# Revit family: ido_seven_d_5650047_arm_001
name_source: partatom
category: Plumbing Fixtures
revit_build: Autodesk Revit 2018 (Build: 20170223_1515(x64)
units: mm (PartAtom-declared; Revit-internal decimal feet)

## family parameters
Always vertical = Yes
Cut with Voids When Loaded = No
Part Type = Normal
Room Calculation Point = No
Round Connector Dimension = Use Radius
Shared = No
Work Plane-Based = No

## types (1)
- ido_seven_d_5650047_arm_001
    Description = connector geom / spherical cord
    MC_R = 55 mm
    Material 1 = Mat1
    RfaVersion = 1.0
    Waste Connection = Yes
    cncShiftX_ = 10000 mm  [stored 32.8084 ft]
    cncShiftY_ = 10000 mm  [stored 32.8084 ft]
    cncShiftZ_ = 10000 mm  [stored 32.8084 ft]
    connectorOrgX = 0 mm  [stored 0 ft]
    connectorOrgY = 0 mm  [stored 0 ft]
    connectorOrgZ = 0 mm  [stored 0 ft]
    magiPartTypeId = 0
    revitCategoryNmb = 240

note: [stored X ft] marks values corroborated as IEEE doubles in the binary element streams (Revit-internal decimal feet)

## geometry (parser evidence)
native form markers: Sweep x3
no freeform markers — native parametric forms only
